# Revit family: Ограждение_Панель 3100
name_source: partatom
category: Специальное оборудование
units: mm (PartAtom-declared; Revit-internal decimal feet)

## family parameters
Общий = Нет
При загрузке вырезать с полостями = Нет
Размер круглого соединителя = Использовать диаметр
Тип детали = Нормальный
Точка расчета площади = Нет

## types (12) — shared parameters
ADSK_Единица измерения = м.
ADSK_Завод-изготовитель = FENSYS
URL = https://www.fensys.ru
Группа модели = Ограждение
Изготовитель = FENSYS
Отступ панели от основания = 70 мм
Ширина панели = 3100 мм

## per-type parameters (varying)
| type | ADSK_Наименование | Глубина столба | Отступ панели | Под бетонирование | С фланцем | С фланцем под В.О. | Ширина столба |
| Панель 3100_Под винт_Столб 60х60 | Ограждение - Панель 3100_Под винт_Столб 60х60 | 60 мм | 30 мм | Нет | Нет | Да | 60 мм |
| Панель 3100_Под бетон_Столб 80х80 | Ограждение - Панель 3100_Под бетон_Столб 80х80 | 80 мм | 40 мм | Да | Нет | Нет | 80 мм |
| Панель 3100_Под бетон_Столб 60х60 | Ограждение - Панель 3100_Под бетон_Столб 60х60 | 60 мм | 30 мм | Да | Нет | Нет | 60 мм |
| Панель 3100_Фланцевое крепление_Столб 80х80 | Ограждение - Панель 3100_Фланцевое крепление_Столб 80х80 | 80 мм | 40 мм | Нет | Да | Нет | 80 мм |
| Панель 3100_Фланцевое крепление_Столб 60х60 | Ограждение - Панель 3100_Фланцевое крепление_Столб 60х60 | 60 мм | 30 мм | Нет | Да | Нет | 60 мм |
| Панель 3100_Фланцевое крепление_Столб 40х60 | Ограждение - Панель 3100_Фланцевое крепление_Столб 40х60 | 60 мм | 20 мм | Нет | Да | Нет | 40 мм |
| Панель 3100_Под бетон_Столб 40х60 | Ограждение - Панель 3100_Под бетон_Столб 40х60 | 60 мм | 20 мм | Да | Нет | Нет | 40 мм |
| Панель 3100_Под винт_Столб 40х60 | Ограждение - Панель 3100_Под винт_Столб 40х60 | 60 мм | 20 мм | Нет | Нет | Да | 40 мм |
| Панель 3100_Под бетон_Столб 60х80 | Ограждение - Панель 3100_Под бетон_Столб 60х80 | 80 мм | 30 мм | Да | Нет | Нет | 60 мм |
| Панель 3100_Под винт_Столб 60х80 | Ограждение - Панель 3100_Под винт_Столб 60х80 | 80 мм | 30 мм | Нет | Нет | Да | 60 мм |
| Панель 3100_Фланцевое крепление_Столб 60х80 | Ограждение - Панель 3100_Фланцевое крепление_Столб 60х80 | 80 мм | 30 мм | Нет | Да | Нет | 60 мм |
| Панель 3100_Под винт_Столб 80х80 | Ограждение - Панель 3100_Под винт_Столб 80х80 | 80 мм | 40 мм | Нет | Нет | Да | 80 мм |
